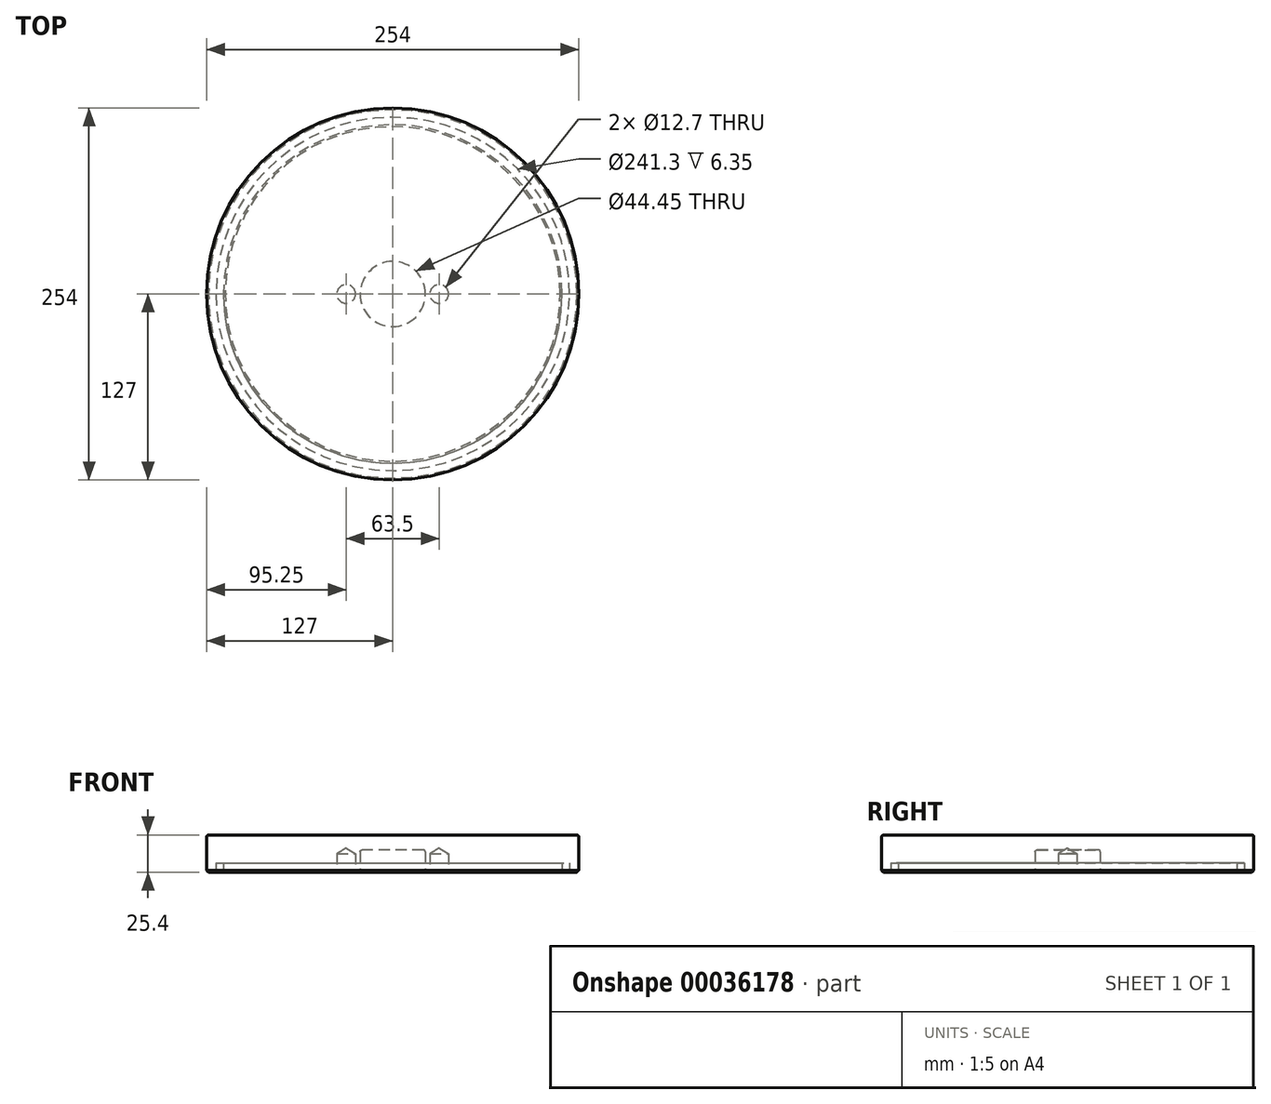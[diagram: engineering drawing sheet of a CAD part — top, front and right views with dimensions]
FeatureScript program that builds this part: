
annotation { "Feature Type Name" : "Feature", "Feature Type Description" : "" }
export const myFeature = defineFeature(function(context is Context, id is Id, definition is map)
    precondition{}
    {
        {
            var Q0;
            Q0=qCreatedBy(makeId("Top.planeOp"),FACE);
            var sketch = newSketch(context, id + "F0", { "sketchPlane" : qUnion([Q0])});
            skCircle(sketch, "E0", {"center": v(0, 0) * mm, "radius": 127 * mm});
            skSolve(sketch);
        }
        {
            var Q0;
            Q0=makeQuery(id+"F0.imprint","IMPRINT",FACE,{"disambiguationData":[TD([[makeQuery(id+"F0.imprint","IMPRINT",EDGE,{"derivedFrom":sQuery(id+"F0.wireOp",EDGE,"E0")}),1.0]])]});
            extrude(context, id + "F1", {"entities" : qUnion([Q0]), "depth" : 25.4 * mm});
        }
        {
            var Q0;
            Q0=makeQuery(id+"F1.opExtrude","CAP_FACE",FACE,{"disambiguationData":[OSD([sQuery(id+"F0.wireOp",EDGE,"E0")])],"isStart":true});
            var sketch = newSketch(context, id + "F2", { "sketchPlane" : qUnion([Q0])});
            skCircle(sketch, "E1", {"center": v(0, 0) * mm, "radius": 120.65 * mm});
            skCircle(sketch, "E2.0", {"center": v(0, 0) * mm, "radius": 115.57 * mm});
            skSolve(sketch);
        }
        {
            var Q0;
            Q0=qCreatedBy(makeId("Top.planeOp"),FACE);
            var sketch = newSketch(context, id + "F3", { "sketchPlane" : qUnion([Q0])});
            skCircle(sketch, "E3", {"center": v(0, 0) * mm, "radius": 22.23 * mm});
            skSolve(sketch);
        }
        {
            var Q0;
            Q0=makeQuery(id+"F2.imprint","IMPRINT",FACE,{"disambiguationData":[TD([[makeQuery(id+"F2.imprint","IMPRINT",EDGE,{"derivedFrom":sQuery(id+"F2.wireOp",EDGE,"E1")}),1.0]])]});
            extrude(context, id + "F4", {"entities" : qUnion([Q0]), "operationType" : NewBodyOperationType.REMOVE, "oppositeDirection" : true, "depth" : 6.35 * mm});
        }
        {
            var Q0;
            Q0=makeQuery(id+"F4.boolean.opBoolean","SPLIT",FACE,{"disambiguationData":[TD([makeQuery(id+"F4.opExtrude","SWEPT_FACE",FACE,{"disambiguationData":[OSD([sQuery(id+"F2.wireOp",EDGE,"E2.0")])]})])],"derivedFrom":makeQuery(id+"F1.opExtrude","CAP_FACE",FACE,{"disambiguationData":[OSD([sQuery(id+"F0.wireOp",EDGE,"E0")])],"isStart":true})});
            var sketch = newSketch(context, id + "F5", { "sketchPlane" : qUnion([Q0])});
            skCircle(sketch, "E4", {"center": v(31.75, 0) * mm, "radius": 6.35 * mm});
            skLineSegment(sketch, "E5", {"start": v(0, 0) * mm, "end": v(31.75, 0) * mm, "construction": true});
            skLineSegment(sketch, "E6", {"start": v(0, 0) * mm, "end": v(0, 45.48) * mm, "construction": true});
            skCircle(sketch, "E7.MirrorC", {"center": v(-31.75, 0) * mm, "radius": 6.35 * mm});
            skSolve(sketch);
        }
        {
            var Q0;
            Q0=makeQuery(id+"F3.imprint","IMPRINT",FACE,{"disambiguationData":[TD([[makeQuery(id+"F3.imprint","IMPRINT",EDGE,{"derivedFrom":sQuery(id+"F3.wireOp",EDGE,"E3")}),1.0]])]});
            extrude(context, id + "F6", {"entities" : qUnion([Q0]), "operationType" : NewBodyOperationType.REMOVE, "depth" : 15.24 * mm});
        }
        {
            var Q0;
            Q0=sQuery(id+"F5.wireOp",VERTEX,"E4.center");
            var Q1;
            Q1=sQuery(id+"F5.wireOp",VERTEX,"E7.MirrorC.center");
            var Q2;
            Q2=makeQuery(id+"F1.opExtrude","SWEPT_BODY",BODY,{"disambiguationData":[OSD([sQuery(id+"F0.wireOp",EDGE,"E0")])]});
            hole(context, id + "F7", {"style" : HoleStyle.SIMPLE, "holeDiameter" : 12.7 * mm, "endStyle" : HoleEndStyle.BLIND, "holeDepth" : 12.7 * mm, "locations" : qUnion([Q0, Q1]), "scope" : qUnion([Q2])});
        }
        {
            var Q0;
            Q0=makeQuery(id+"F6.boolean.opBoolean","COPY",EDGE,{"derivedFrom":makeQuery(id+"F6.opExtrude","CAP_EDGE",EDGE,{"disambiguationData":[OSD([sQuery(id+"F3.wireOp",EDGE,"E3")])],"isStart":false})});
            var Q1;
            Q1=makeQuery(id+"F6.boolean.opBoolean","COPY",FACE,{"derivedFrom":makeQuery(id+"F6.opExtrude","CAP_FACE",FACE,{"disambiguationData":[OSD([sQuery(id+"F3.wireOp",EDGE,"E3")])],"isStart":false})});
            var Q2;
            Q2=makeQuery(id+"F1.opExtrude","CAP_FACE",FACE,{"disambiguationData":[OSD([sQuery(id+"F0.wireOp",EDGE,"E0")])],"isStart":false});
            fillet(context, id + "F8", {"entities" : qUnion([Q0, Q1, Q2]), "radius" : 1.27 * mm, "tangentPropagation" : true, "allowEdgeOverflow" : false});
        }
        {
            var Q0;
            Q0=makeQuery(id+"F6.boolean.opBoolean","COPY",EDGE,{"derivedFrom":makeQuery(id+"F6.opExtrude","CAP_EDGE",EDGE,{"disambiguationData":[OSD([sQuery(id+"F3.wireOp",EDGE,"E3")])],"isStart":true})});
            var Q1;
            Q1=makeQuery(id+"F7.hole-0.boolean.opBoolean","COPY",EDGE,{"derivedFrom":makeQuery(id+"F7.hole-0.opRevolve","SWEPT_EDGE",EDGE,{"disambiguationData":[OSD([sQuery(id+"F7.hole-0.sketch.wireOp",EDGE,"core_line_2"),sQuery(id+"F7.hole-0.sketch.wireOp",EDGE,"core_line_3")])]})});
            var Q2;
            Q2=makeQuery(id+"F7.hole-1.boolean.opBoolean","COPY",EDGE,{"derivedFrom":makeQuery(id+"F7.hole-1.opRevolve","SWEPT_EDGE",EDGE,{"disambiguationData":[OSD([sQuery(id+"F7.hole-1.sketch.wireOp",EDGE,"core_line_2"),sQuery(id+"F7.hole-1.sketch.wireOp",EDGE,"core_line_3")])]})});
            var Q3;
            Q3=makeQuery(id+"F4.boolean.opBoolean","COPY",EDGE,{"derivedFrom":makeQuery(id+"F4.opExtrude","CAP_EDGE",EDGE,{"disambiguationData":[OSD([sQuery(id+"F2.wireOp",EDGE,"E2.0")])],"isStart":true})});
            var Q4;
            Q4=makeQuery(id+"F4.boolean.opBoolean","COPY",EDGE,{"derivedFrom":makeQuery(id+"F4.opExtrude","CAP_EDGE",EDGE,{"disambiguationData":[OSD([sQuery(id+"F2.wireOp",EDGE,"E1")])],"isStart":true})});
            var Q5;
            Q5=makeQuery(id+"F1.opExtrude","CAP_EDGE",EDGE,{"disambiguationData":[OSD([sQuery(id+"F0.wireOp",EDGE,"E0")])],"isStart":true});
            chamfer(context, id + "F9", {"entities" : qUnion([Q0, Q1, Q2, Q3, Q4, Q5]), "width" : 1.27 * mm, "tangentPropagation" : true});
        }
    });
